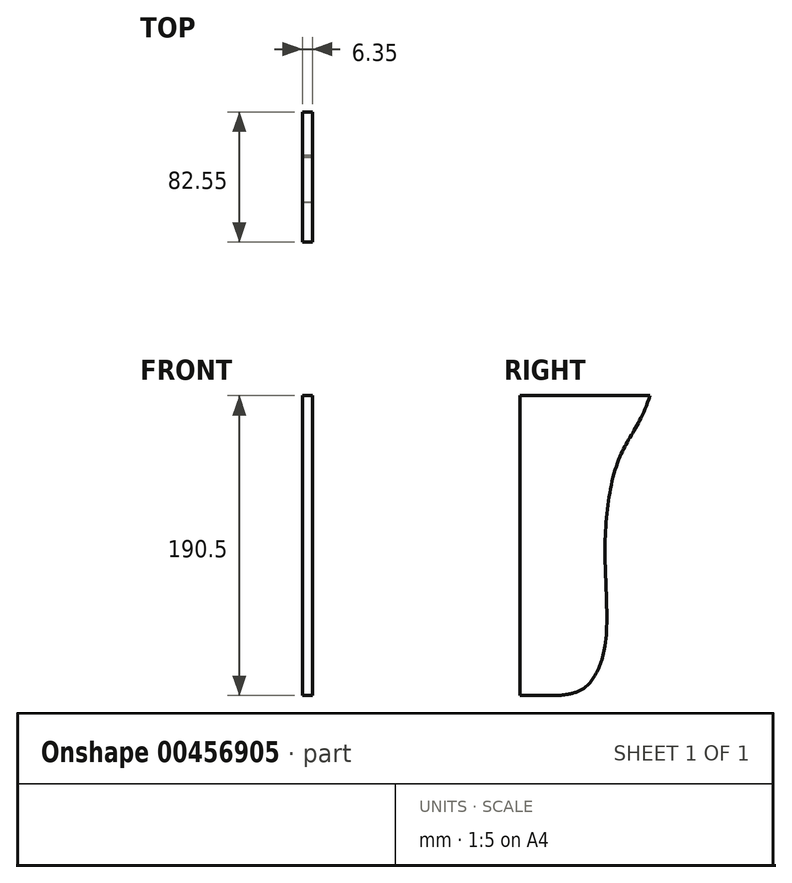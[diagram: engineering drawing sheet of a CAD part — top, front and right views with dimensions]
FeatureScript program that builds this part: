
annotation { "Feature Type Name" : "Feature", "Feature Type Description" : "" }
export const myFeature = defineFeature(function(context is Context, id is Id, definition is map)
    precondition{}
    {
        {
            var Q0;
            Q0=qCreatedBy(makeId("Right.planeOp"),FACE);
            var sketch = newSketch(context, id + "F0", { "sketchPlane" : qUnion([Q0])});
            skLineSegment(sketch, "E0.bottom", {"start": v(-94.16, 80.5) * mm, "end": v(-11.6, 80.5) * mm});
            skLineSegment(sketch, "E0.top", {"start": v(-94.16, -110) * mm, "end": v(-11.6, -110) * mm});
            skLineSegment(sketch, "E0.left", {"start": v(-94.16, 80.5) * mm, "end": v(-94.16, -110) * mm});
            skLineSegment(sketch, "E1", {"start": v(-11.6, -110) * mm, "end": v(-11.6, 80.5) * mm});
            skSolve(sketch);
        }
        {
            var Q0;
            Q0=makeQuery(id+"F0.imprint","IMPRINT",FACE,{"disambiguationData":[TD([[makeQuery(id+"F0.imprint","IMPRINT",EDGE,{"derivedFrom":sQuery(id+"F0.wireOp",EDGE,"E0.bottom")}),-1.0]])]});
            extrude(context, id + "F1", {"entities" : qUnion([Q0]), "depth" : 6.35 * mm});
        }
        {
            var Q0;
            Q0=makeQuery(id+"F1.opExtrude","CAP_FACE",FACE,{"disambiguationData":[OSD([sQuery(id+"F0.wireOp",EDGE,"E0.bottom"),sQuery(id+"F0.wireOp",EDGE,"E0.top"),sQuery(id+"F0.wireOp",EDGE,"E0.left"),sQuery(id+"F0.wireOp",EDGE,"E1")])],"isStart":false});
            var sketch = newSketch(context, id + "F2", { "sketchPlane" : qUnion([Q0])});
            skPoint(sketch, "E2", {"position": v(-68.76, -110) * mm});
            skPoint(sketch, "E3", {"position": v(-52.88, -110) * mm});
            skPoint(sketch, "E4", {"position": v(-30.66, -110) * mm});
            skPoint(sketch, "E5", {"position": v(-68.76, 80.5) * mm});
            skPoint(sketch, "E6", {"position": v(-52.88, 80.5) * mm});
            skPoint(sketch, "E7", {"position": v(-30.66, 80.5) * mm});
            skPoint(sketch, "E8", {"position": v(-11.6, -78.47) * mm});
            skPoint(sketch, "E9", {"position": v(-11.6, -16.94) * mm});
            skPoint(sketch, "E10", {"position": v(-11.6, 41.7) * mm});
            skLineSegment(sketch, "E11", {"start": v(-68.76, -110) * mm, "end": v(-68.76, 80.5) * mm});
            skLineSegment(sketch, "E12", {"start": v(-52.88, 80.5) * mm, "end": v(-52.88, -110) * mm});
            skLineSegment(sketch, "E13", {"start": v(-30.66, -110) * mm, "end": v(-30.66, 80.5) * mm});
            skLineSegment(sketch, "E14", {"start": v(-11.6, -78.47) * mm, "end": v(-68.76, -78.47) * mm});
            skLineSegment(sketch, "E15", {"start": v(-11.6, -16.94) * mm, "end": v(-68.76, -16.94) * mm});
            skLineSegment(sketch, "E16", {"start": v(-11.6, 41.7) * mm, "end": v(-68.76, 41.7) * mm});
            skPoint(sketch, "E17", {"position": v(-11.6, -104.91) * mm});
            skLineSegment(sketch, "E18", {"start": v(-11.6, -104.91) * mm, "end": v(-68.76, -104.91) * mm});
            skFitSpline(sketch, "E19", {"points": [v(-68.76, -110) * mm, v(-52.88, -104.91) * mm, v(-40.18, -78.47) * mm, v(-40.18, -16.94) * mm, v(-30.66, 41.7) * mm, v(-11.6, 80.5) * mm], "startDerivative": vector(133.75, 18.49) * mm, "endDerivative": vector(81, 260.47) * mm});
            skSolve(sketch);
        }
        {
            var Q0;
            Q0=makeQuery(id+"F2.imprint","IMPRINT",FACE,{"disambiguationData":[TD([[makeQuery(id+"F2.imprint","IMPRINT",EDGE,{"derivedFrom":sQuery(id+"F2.wireOp",EDGE,"2420c2ae-a728-462d-96e0-0812c52a9f00")}),-1.0]])]});
            var Q1;
            {var subQ0=sQuery(id+"F2.wireOp",EDGE,"E18");var subQ1=sQuery(id+"F2.wireOp",EDGE,"E13");var subQ2=makeQuery(id+"F2.imprint","INTERSECT",VERTEX,{"derivedFrom":[subQ1,subQ0]});Q1=makeQuery(id+"F2.imprint","IMPRINT",FACE,{"disambiguationData":[TD([[makeQuery(id+"F2.imprint","IMPRINT",EDGE,{"disambiguationData":[TD([[subQ2,-1.0]])],"derivedFrom":subQ1}),1.0]])]});}
            var Q2;
            {var subQ1=makeQuery(id+"F1.opExtrude","CAP_EDGE",EDGE,{"disambiguationData":[OSD([sQuery(id+"F0.wireOp",EDGE,"E0.top")])],"isStart":false});var subQ5=sQuery(id+"F2.wireOp",EDGE,"E13");var subQ6=makeQuery(id+"F2.imprint","INTERSECT",VERTEX,{"derivedFrom":[subQ1,subQ5]});Q2=makeQuery(id+"F2.imprint","IMPRINT",FACE,{"disambiguationData":[TD([[makeQuery(id+"F2.imprint","IMPRINT",EDGE,{"disambiguationData":[TD([[subQ6,-1.0]])],"derivedFrom":subQ5}),1.0]])]});}
            var Q3;
            {var subQ0=sQuery(id+"F2.wireOp",EDGE,"E12");var subQ1=makeQuery(id+"F1.opExtrude","CAP_EDGE",EDGE,{"disambiguationData":[OSD([sQuery(id+"F0.wireOp",EDGE,"E0.top")])],"isStart":false});var subQ2=makeQuery(id+"F2.imprint","INTERSECT",VERTEX,{"derivedFrom":[subQ1,subQ0]});Q3=makeQuery(id+"F2.imprint","IMPRINT",FACE,{"disambiguationData":[TD([[makeQuery(id+"F2.imprint","IMPRINT",EDGE,{"disambiguationData":[TD([[subQ2,1.0]])],"derivedFrom":subQ0}),-1.0]])]});}
            var Q4;
            {var subQ0=sQuery(id+"F2.wireOp",EDGE,"E13");var subQ1=makeQuery(id+"F1.opExtrude","CAP_EDGE",EDGE,{"disambiguationData":[OSD([sQuery(id+"F0.wireOp",EDGE,"E0.top")])],"isStart":false});var subQ2=makeQuery(id+"F2.imprint","INTERSECT",VERTEX,{"derivedFrom":[subQ1,subQ0]});Q4=makeQuery(id+"F2.imprint","IMPRINT",FACE,{"disambiguationData":[TD([[makeQuery(id+"F2.imprint","IMPRINT",EDGE,{"disambiguationData":[TD([[subQ2,-1.0]])],"derivedFrom":subQ0}),-1.0]])]});}
            var Q5;
            {var subQ0=sQuery(id+"F2.wireOp",EDGE,"E18");var subQ1=sQuery(id+"F2.wireOp",EDGE,"E13");var subQ2=makeQuery(id+"F2.imprint","INTERSECT",VERTEX,{"derivedFrom":[subQ1,subQ0]});Q5=makeQuery(id+"F2.imprint","IMPRINT",FACE,{"disambiguationData":[TD([[makeQuery(id+"F2.imprint","IMPRINT",EDGE,{"disambiguationData":[TD([[subQ2,-1.0]])],"derivedFrom":subQ1}),-1.0]])]});}
            var Q6;
            {var subQ0=sQuery(id+"F2.wireOp",EDGE,"E14");var subQ1=sQuery(id+"F2.wireOp",EDGE,"E13");var subQ2=makeQuery(id+"F2.imprint","INTERSECT",VERTEX,{"derivedFrom":[subQ1,subQ0]});Q6=makeQuery(id+"F2.imprint","IMPRINT",FACE,{"disambiguationData":[TD([[makeQuery(id+"F2.imprint","IMPRINT",EDGE,{"disambiguationData":[TD([[subQ2,-1.0]])],"derivedFrom":subQ1}),-1.0]])]});}
            var Q7;
            {var subQ0=sQuery(id+"F2.wireOp",EDGE,"E14");var subQ1=sQuery(id+"F2.wireOp",EDGE,"E13");var subQ2=makeQuery(id+"F2.imprint","INTERSECT",VERTEX,{"derivedFrom":[subQ1,subQ0]});Q7=makeQuery(id+"F2.imprint","IMPRINT",FACE,{"disambiguationData":[TD([[makeQuery(id+"F2.imprint","IMPRINT",EDGE,{"disambiguationData":[TD([[subQ2,-1.0]])],"derivedFrom":subQ1}),1.0]])]});}
            var Q8;
            {var subQ0=sQuery(id+"F2.wireOp",EDGE,"E15");var subQ1=sQuery(id+"F2.wireOp",EDGE,"E13");var subQ2=makeQuery(id+"F2.imprint","INTERSECT",VERTEX,{"derivedFrom":[subQ1,subQ0]});Q8=makeQuery(id+"F2.imprint","IMPRINT",FACE,{"disambiguationData":[TD([[makeQuery(id+"F2.imprint","IMPRINT",EDGE,{"disambiguationData":[TD([[subQ2,-1.0]])],"derivedFrom":subQ0}),-1.0]])]});}
            var Q9;
            {var subQ0=sQuery(id+"F2.wireOp",EDGE,"E15");var subQ5=makeQuery(id+"F1.opExtrude","CAP_EDGE",EDGE,{"disambiguationData":[OSD([sQuery(id+"F0.wireOp",EDGE,"E1")])],"isStart":false});var subQ7=makeQuery(id+"F2.imprint","INTERSECT",VERTEX,{"derivedFrom":[subQ5,subQ0]});Q9=makeQuery(id+"F2.imprint","IMPRINT",FACE,{"disambiguationData":[TD([[makeQuery(id+"F2.imprint","IMPRINT",EDGE,{"disambiguationData":[TD([[subQ7,-1.0]])],"derivedFrom":subQ0}),-1.0]])]});}
            var Q10;
            {var subQ0=sQuery(id+"F2.wireOp",EDGE,"E16");var subQ1=makeQuery(id+"F1.opExtrude","CAP_EDGE",EDGE,{"disambiguationData":[OSD([sQuery(id+"F0.wireOp",EDGE,"E1")])],"isStart":false});var subQ2=makeQuery(id+"F2.imprint","INTERSECT",VERTEX,{"derivedFrom":[subQ1,subQ0]});Q10=makeQuery(id+"F2.imprint","IMPRINT",FACE,{"disambiguationData":[TD([[makeQuery(id+"F2.imprint","IMPRINT",EDGE,{"disambiguationData":[TD([[subQ2,-1.0]])],"derivedFrom":subQ0}),-1.0]])]});}
            extrude(context, id + "F3", {"entities" : qUnion([Q0, Q1, Q2, Q3, Q4, Q5, Q6, Q7, Q8, Q9, Q10]), "operationType" : NewBodyOperationType.REMOVE, "oppositeDirection" : true, "depth" : 12.7 * mm});
        }
    });
